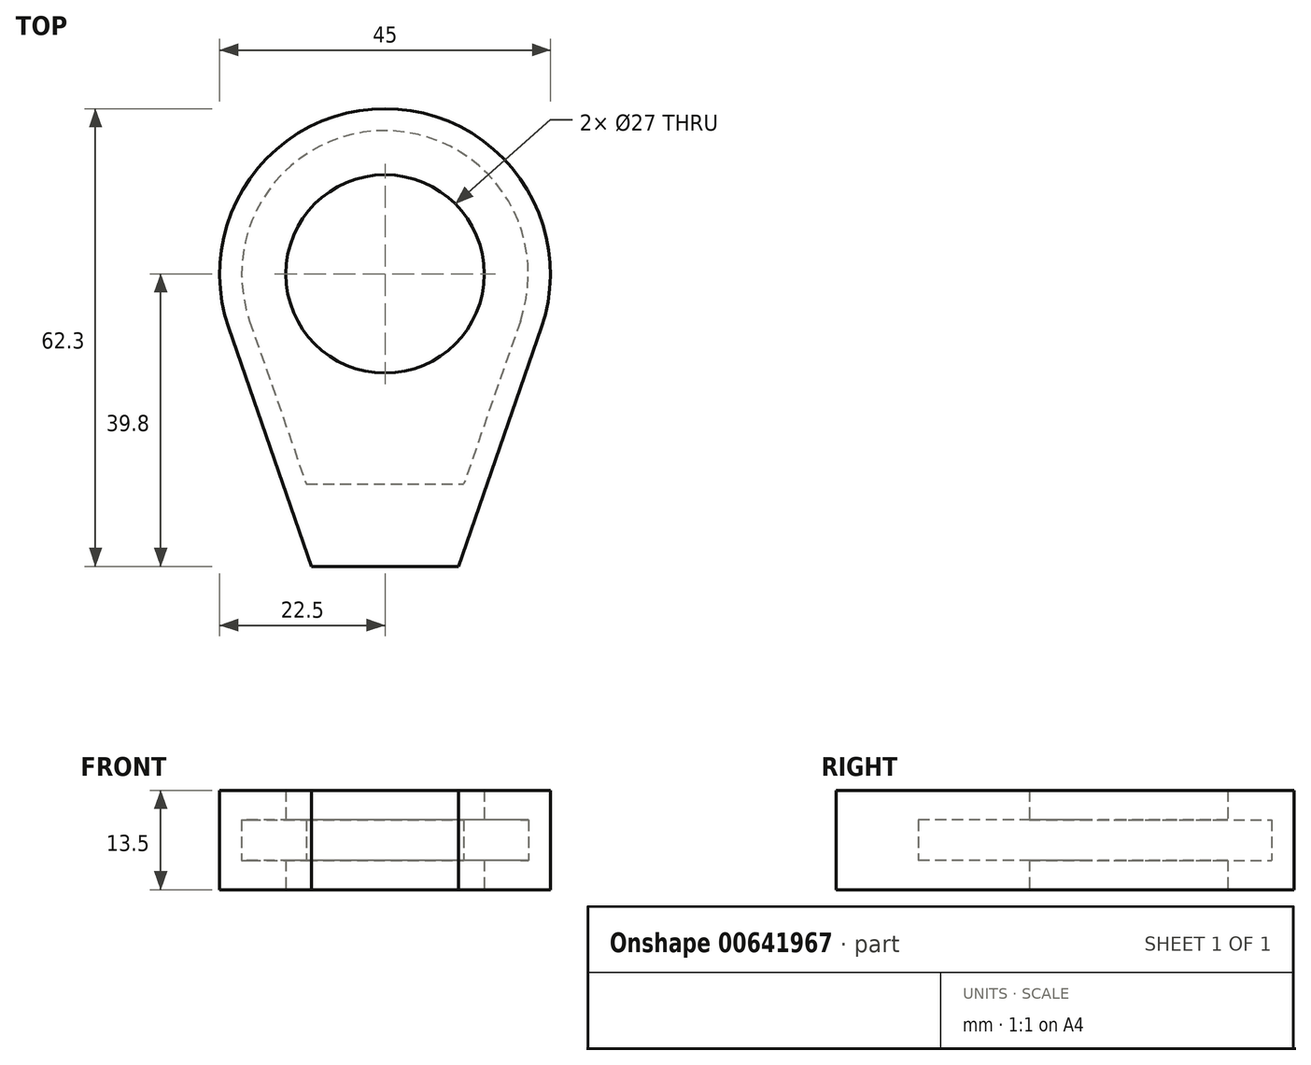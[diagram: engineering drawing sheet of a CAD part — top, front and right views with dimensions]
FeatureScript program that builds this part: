
annotation { "Feature Type Name" : "Feature", "Feature Type Description" : "" }
export const myFeature = defineFeature(function(context is Context, id is Id, definition is map)
    precondition{}
    {
        {
            var Q0;
            Q0=qCreatedBy(makeId("Top.planeOp"),FACE);
            var sketch = newSketch(context, id + "F0", { "sketchPlane" : qUnion([Q0])});
            skCircle(sketch, "E0", {"center": v(0, 0) * mm, "radius": 22.5 * mm});
            skCircle(sketch, "E1", {"center": v(0, 0) * mm, "radius": 13.5 * mm});
            skLineSegment(sketch, "E2", {"start": v(0, -39.8) * mm, "end": v(10, -39.8) * mm});
            skLineSegment(sketch, "E3", {"start": v(0, -39.8) * mm, "end": v(-10, -39.8) * mm});
            skLineSegment(sketch, "E4", {"start": v(-10, -39.8) * mm, "end": v(-21.26, -7.38) * mm});
            skLineSegment(sketch, "E5", {"start": v(21.26, -7.38) * mm, "end": v(10, -39.8) * mm});
            skCircle(sketch, "E6", {"center": v(0, 0) * mm, "radius": 17.5 * mm, "construction": true});
            skCircle(sketch, "E7", {"center": v(0, 0) * mm, "radius": 14.5 * mm, "construction": true});
            skPoint(sketch, "E8", {"position": v(0, 14.5) * mm});
            skPoint(sketch, "E9", {"position": v(0, 17.5) * mm});
            skPoint(sketch, "E10.1.0", {"position": v(-5.99, 16.44) * mm});
            skPoint(sketch, "E10.2.0", {"position": v(-11.25, 13.4) * mm});
            skPoint(sketch, "E10.3.0", {"position": v(-15.16, 8.75) * mm});
            skPoint(sketch, "E10.4.0", {"position": v(-17.23, 3.04) * mm});
            skPoint(sketch, "E10.5.0", {"position": v(-17.23, -3.04) * mm});
            skPoint(sketch, "E10.6.0", {"position": v(-15.16, -8.75) * mm});
            skPoint(sketch, "E10.7.0", {"position": v(-11.25, -13.4) * mm});
            skPoint(sketch, "E10.8.0", {"position": v(-5.99, -16.44) * mm});
            skPoint(sketch, "E10.9.0", {"position": v(0, -17.5) * mm});
            skPoint(sketch, "E10.10.0", {"position": v(5.99, -16.44) * mm});
            skPoint(sketch, "E10.11.0", {"position": v(11.25, -13.4) * mm});
            skPoint(sketch, "E10.12.0", {"position": v(15.16, -8.75) * mm});
            skPoint(sketch, "E10.13.0", {"position": v(17.23, -3.04) * mm});
            skPoint(sketch, "E10.14.0", {"position": v(17.23, 3.04) * mm});
            skPoint(sketch, "E10.15.0", {"position": v(15.16, 8.75) * mm});
            skPoint(sketch, "E10.16.0", {"position": v(11.25, 13.4) * mm});
            skPoint(sketch, "E10.17.0", {"position": v(5.99, 16.44) * mm});
            skPoint(sketch, "E11.1.0", {"position": v(-4.96, 13.63) * mm});
            skPoint(sketch, "E11.2.0", {"position": v(-9.32, 11.1) * mm});
            skPoint(sketch, "E11.3.0", {"position": v(-12.56, 7.25) * mm});
            skPoint(sketch, "E11.4.0", {"position": v(-14.28, 2.52) * mm});
            skPoint(sketch, "E11.5.0", {"position": v(-14.28, -2.52) * mm});
            skPoint(sketch, "E11.6.0", {"position": v(-12.56, -7.25) * mm});
            skPoint(sketch, "E11.7.0", {"position": v(-9.32, -11.1) * mm});
            skPoint(sketch, "E11.8.0", {"position": v(-4.96, -13.63) * mm});
            skPoint(sketch, "E11.9.0", {"position": v(0, -14.5) * mm});
            skPoint(sketch, "E11.10.0", {"position": v(4.96, -13.63) * mm});
            skPoint(sketch, "E11.11.0", {"position": v(9.32, -11.1) * mm});
            skPoint(sketch, "E11.12.0", {"position": v(12.56, -7.25) * mm});
            skPoint(sketch, "E11.13.0", {"position": v(14.28, -2.52) * mm});
            skPoint(sketch, "E11.14.0", {"position": v(14.28, 2.52) * mm});
            skPoint(sketch, "E11.15.0", {"position": v(12.56, 7.25) * mm});
            skPoint(sketch, "E11.16.0", {"position": v(9.32, 11.1) * mm});
            skPoint(sketch, "E11.17.0", {"position": v(4.96, 13.63) * mm});
            skLineSegment(sketch, "E12", {"start": v(0, -17.5) * mm, "end": v(4.96, -13.63) * mm, "construction": true});
            skLineSegment(sketch, "E13", {"start": v(5.99, -16.44) * mm, "end": v(9.32, -11.1) * mm, "construction": true});
            skLineSegment(sketch, "E14", {"start": v(11.25, -13.4) * mm, "end": v(12.56, -7.25) * mm, "construction": true});
            skLineSegment(sketch, "E15", {"start": v(15.16, -8.75) * mm, "end": v(14.28, -2.52) * mm, "construction": true});
            skLineSegment(sketch, "E16", {"start": v(0, -17.5) * mm, "end": v(0, -14.5) * mm, "construction": true});
            skLineSegment(sketch, "E17", {"start": v(5.99, -16.44) * mm, "end": v(4.96, -13.63) * mm, "construction": true});
            skLineSegment(sketch, "E18", {"start": v(11.25, -13.4) * mm, "end": v(9.32, -11.1) * mm, "construction": true});
            skLineSegment(sketch, "E19", {"start": v(15.16, -8.75) * mm, "end": v(12.56, -7.25) * mm, "construction": true});
            skLineSegment(sketch, "E20", {"start": v(17.23, -3.04) * mm, "end": v(14.28, -2.52) * mm, "construction": true});
            skLineSegment(sketch, "E21", {"start": v(17.23, -3.04) * mm, "end": v(14.28, 2.52) * mm, "construction": true});
            skLineSegment(sketch, "E22", {"start": v(-5.99, -16.44) * mm, "end": v(0, -14.5) * mm, "construction": true});
            skLineSegment(sketch, "E23", {"start": v(-11.25, -13.4) * mm, "end": v(-4.96, -13.63) * mm, "construction": true});
            skLineSegment(sketch, "E24", {"start": v(-15.16, -8.75) * mm, "end": v(-9.32, -11.1) * mm, "construction": true});
            skLineSegment(sketch, "E25", {"start": v(-9.32, -11.1) * mm, "end": v(-11.25, -13.4) * mm, "construction": true});
            skLineSegment(sketch, "E26", {"start": v(-4.96, -13.63) * mm, "end": v(-5.99, -16.44) * mm, "construction": true});
            skLineSegment(sketch, "E27", {"start": v(-12.56, -7.25) * mm, "end": v(-15.16, -8.75) * mm, "construction": true});
            skLineSegment(sketch, "E28", {"start": v(-17.23, -3.04) * mm, "end": v(-12.56, -7.25) * mm, "construction": true});
            skLineSegment(sketch, "E29", {"start": v(-17.23, -3.04) * mm, "end": v(-14.28, -2.52) * mm, "construction": true});
            skLineSegment(sketch, "E30", {"start": v(-14.28, -2.52) * mm, "end": v(-17.23, 3.04) * mm, "construction": true});
            skLineSegment(sketch, "E31", {"start": v(-14.28, 2.52) * mm, "end": v(-17.23, 3.04) * mm, "construction": true});
            skLineSegment(sketch, "E32", {"start": v(-14.28, 2.52) * mm, "end": v(-15.16, 8.75) * mm, "construction": true});
            skLineSegment(sketch, "E33", {"start": v(-12.56, 7.25) * mm, "end": v(-15.16, 8.75) * mm, "construction": true});
            skLineSegment(sketch, "E34", {"start": v(-11.25, 13.4) * mm, "end": v(-12.56, 7.25) * mm, "construction": true});
            skLineSegment(sketch, "E35", {"start": v(-11.25, 13.4) * mm, "end": v(-9.32, 11.1) * mm, "construction": true});
            skLineSegment(sketch, "E36", {"start": v(-5.99, 16.44) * mm, "end": v(-9.32, 11.1) * mm, "construction": true});
            skLineSegment(sketch, "E37", {"start": v(-4.96, 13.63) * mm, "end": v(-5.99, 16.44) * mm, "construction": true});
            skLineSegment(sketch, "E38", {"start": v(0, 17.5) * mm, "end": v(0, 14.5) * mm, "construction": true});
            skLineSegment(sketch, "E39", {"start": v(0, 17.5) * mm, "end": v(-4.96, 13.63) * mm, "construction": true});
            skLineSegment(sketch, "E40", {"start": v(5.99, 16.44) * mm, "end": v(0, 14.5) * mm, "construction": true});
            skLineSegment(sketch, "E41", {"start": v(4.96, 13.63) * mm, "end": v(5.99, 16.44) * mm, "construction": true});
            skLineSegment(sketch, "E42", {"start": v(11.25, 13.4) * mm, "end": v(4.96, 13.63) * mm, "construction": true});
            skLineSegment(sketch, "E43", {"start": v(15.16, 8.75) * mm, "end": v(9.32, 11.1) * mm, "construction": true});
            skLineSegment(sketch, "E44", {"start": v(17.23, 3.04) * mm, "end": v(12.56, 7.25) * mm, "construction": true});
            skLineSegment(sketch, "E45", {"start": v(14.28, 2.52) * mm, "end": v(17.23, 3.04) * mm, "construction": true});
            skLineSegment(sketch, "E46", {"start": v(15.16, 8.75) * mm, "end": v(12.56, 7.25) * mm, "construction": true});
            skLineSegment(sketch, "E47", {"start": v(11.25, 13.4) * mm, "end": v(9.32, 11.1) * mm, "construction": true});
            skSolve(sketch);
        }
        {
            var Q0;
            Q0=makeQuery(id+"F0.imprint","IMPRINT",FACE,{"disambiguationData":[TD([[makeQuery(id+"F0.imprint","IMPRINT",EDGE,{"derivedFrom":sQuery(id+"F0.wireOp",EDGE,"E1")}),-1.0]])]});
            var Q1;
            Q1=makeQuery(id+"F0.imprint","IMPRINT",FACE,{"disambiguationData":[TD([[makeQuery(id+"F0.imprint","IMPRINT",EDGE,{"derivedFrom":sQuery(id+"F0.wireOp",EDGE,"E2")}),1.0]])]});
            extrude(context, id + "F1", {"entities" : qUnion([Q0, Q1]), "depth" : 4 * mm, "offsetDistance" : 25 * mm});
        }
        {
            var Q0;
            Q0=makeQuery(id+"F1.opExtrude","CAP_FACE",FACE,{"disambiguationData":[OSD([sQuery(id+"F0.wireOp",EDGE,"E0"),sQuery(id+"F0.wireOp",EDGE,"E1"),sQuery(id+"F0.wireOp",EDGE,"E2"),sQuery(id+"F0.wireOp",EDGE,"E3"),sQuery(id+"F0.wireOp",EDGE,"E4"),sQuery(id+"F0.wireOp",EDGE,"E5")])],"isStart":false});
            var sketch = newSketch(context, id + "F2", { "sketchPlane" : qUnion([Q0])});
            skCircle(sketch, "E48", {"center": v(0, 0) * mm, "radius": 17.5 * mm, "construction": true});
            skCircle(sketch, "E49", {"center": v(0, 0) * mm, "radius": 19.5 * mm});
            skLineSegment(sketch, "E50", {"start": v(-18.42, -6.4) * mm, "end": v(-10.7, -28.61) * mm});
            skLineSegment(sketch, "E51", {"start": v(18.42, -6.4) * mm, "end": v(10.7, -28.61) * mm});
            skLineSegment(sketch, "E52", {"start": v(-10.7, -28.61) * mm, "end": v(10.7, -28.61) * mm});
            skLineSegment(sketch, "E53", {"start": v(4.84, -13.73) * mm, "end": v(-2.76, -20.78) * mm, "construction": true});
            skLineSegment(sketch, "E54", {"start": v(4.84, -13.73) * mm, "end": v(5.85, -16.5) * mm, "construction": true});
            skLineSegment(sketch, "E55", {"start": v(5.85, -16.5) * mm, "end": v(-0.92, -22.77) * mm, "construction": true});
            skCircle(sketch, "E56", {"center": v(-4.78, -24.5) * mm, "radius": 1.36 * mm, "construction": true});
            skArc(sketch, "E57", {"start": v(-5.86, -22.92) * mm, "mid": v(-6.19, -25.81) * mm, "end": v(-3.28, -25.7) * mm, "construction": true});
            skLineSegment(sketch, "E58", {"start": v(-3.28, -25.7) * mm, "end": v(-0.92, -22.77) * mm, "construction": true});
            skLineSegment(sketch, "E59", {"start": v(-0.92, -22.77) * mm, "end": v(-2.76, -20.78) * mm, "construction": true});
            skLineSegment(sketch, "E60", {"start": v(-5.86, -22.92) * mm, "end": v(-2.76, -20.78) * mm, "construction": true});
            skSolve(sketch);
        }
        {
            var Q0;
            {var subQ1=sQuery(id+"F2.wireOp",EDGE,"E50");Q0=makeQuery(id+"F2.imprint","IMPRINT",FACE,{"disambiguationData":[TD([[makeQuery(id+"F2.imprint","IMPRINT",EDGE,{"derivedFrom":subQ1}),-1.0]])]});}
            extrude(context, id + "F3", {"entities" : qUnion([Q0]), "operationType" : NewBodyOperationType.ADD, "depth" : 5.5 * mm, "offsetDistance" : 25 * mm});
        }
        {
            var Q0;
            Q0=makeQuery(id+"F3.opExtrude","CAP_FACE",FACE,{"disambiguationData":[OSD([sQuery(id+"F0.wireOp",EDGE,"E0"),sQuery(id+"F0.wireOp",EDGE,"E2"),sQuery(id+"F0.wireOp",EDGE,"E3"),sQuery(id+"F0.wireOp",EDGE,"E4"),sQuery(id+"F0.wireOp",EDGE,"E5"),sQuery(id+"F2.wireOp",EDGE,"E49"),sQuery(id+"F2.wireOp",EDGE,"E50"),sQuery(id+"F2.wireOp",EDGE,"E51"),sQuery(id+"F2.wireOp",EDGE,"E52")])],"isStart":false});
            var sketch = newSketch(context, id + "F4", { "sketchPlane" : qUnion([Q0])});
            skArc(sketch, "E61.0", {"start": v(18.42, -6.4) * mm, "mid": v(0, 19.5) * mm, "end": v(-18.42, -6.4) * mm});
            skCircle(sketch, "E62.0", {"center": v(0, 0) * mm, "radius": 22.5 * mm});
            skLineSegment(sketch, "E63.0", {"start": v(-10, -39.8) * mm, "end": v(-21.26, -7.38) * mm});
            skLineSegment(sketch, "E63.1", {"start": v(0, -39.8) * mm, "end": v(-10, -39.8) * mm});
            skLineSegment(sketch, "E63.2", {"start": v(0, -39.8) * mm, "end": v(10, -39.8) * mm});
            skLineSegment(sketch, "E63.3", {"start": v(21.26, -7.38) * mm, "end": v(10, -39.8) * mm});
            skLineSegment(sketch, "E64", {"start": v(-21.26, -7.38) * mm, "end": v(-10, -39.8) * mm});
            skLineSegment(sketch, "E65", {"start": v(10, -39.8) * mm, "end": v(21.26, -7.38) * mm});
            skCircle(sketch, "E66.0", {"center": v(0, 0) * mm, "radius": 13.5 * mm});
            skPoint(sketch, "E67", {"position": v(0, 13.5) * mm});
            skSolve(sketch);
        }
        {
            var Q0;
            {var subQ0=sQuery(id+"F4.wireOp",EDGE,"E61.0");Q0=makeQuery(id+"F4.imprint","IMPRINT",FACE,{"disambiguationData":[TD([[makeQuery(id+"F4.imprint","IMPRINT",EDGE,{"derivedFrom":subQ0}),1.0]])]});}
            var Q1;
            {var subQ7=sQuery(id+"F4.wireOp",EDGE,"E61.0");Q1=makeQuery(id+"F4.imprint","IMPRINT",FACE,{"disambiguationData":[TD([[makeQuery(id+"F4.imprint","IMPRINT",EDGE,{"derivedFrom":subQ7}),-1.0]])]});}
            var Q2;
            Q2=makeQuery(id+"F4.imprint","IMPRINT",FACE,{"disambiguationData":[TD([[makeQuery(id+"F4.imprint","IMPRINT",EDGE,{"derivedFrom":sQuery(id+"F4.wireOp",EDGE,"E63.1")}),-1.0]])]});
            var Q3;
            {var subQ5=makeQuery(id+"F3.opExtrude","CAP_EDGE",EDGE,{"disambiguationData":[OSD([sQuery(id+"F2.wireOp",EDGE,"E52")])],"isStart":false});Q3=makeQuery(id+"F4.imprint","IMPRINT",FACE,{"disambiguationData":[TD([[makeQuery(id+"F4.imprint","IMPRINT",EDGE,{"derivedFrom":subQ5}),1.0]])]});}
            var Q4;
            Q4 = qSketchRegion(id + "F0", true);
            extrude(context, id + "F5", {"entities" : qUnion([Q0, Q1, Q2, Q3, Q4]), "operationType" : NewBodyOperationType.ADD, "depth" : 4 * mm, "offsetDistance" : 25 * mm});
        }
    });
